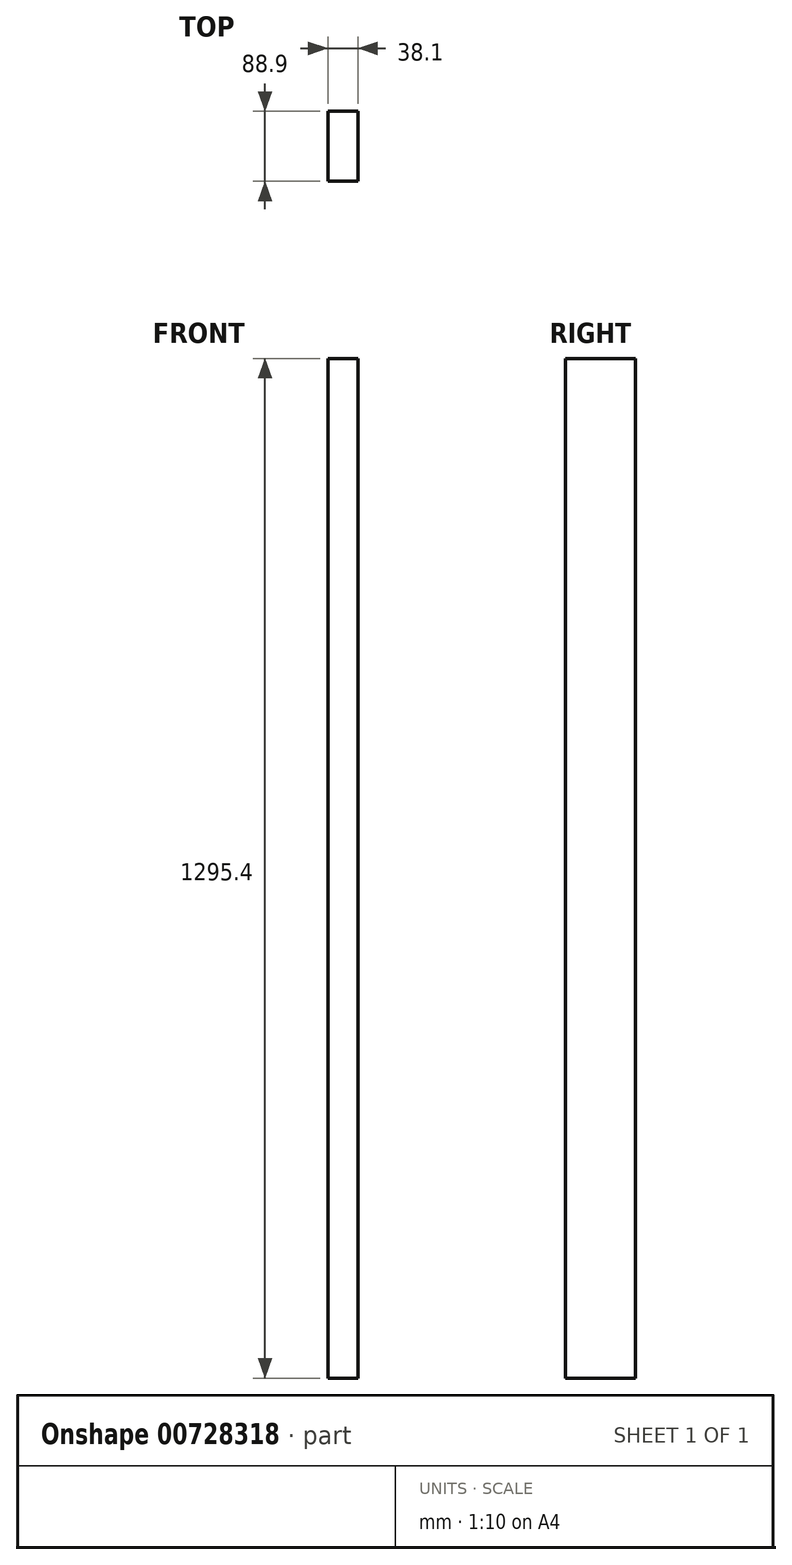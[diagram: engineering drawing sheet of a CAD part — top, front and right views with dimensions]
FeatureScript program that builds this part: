
annotation { "Feature Type Name" : "Feature", "Feature Type Description" : "" }
export const myFeature = defineFeature(function(context is Context, id is Id, definition is map)
    precondition{}
    {
        {
            var Q0;
            Q0=qCreatedBy(makeId("Front.planeOp"),FACE);
            var sketch = newSketch(context, id + "F0", { "sketchPlane" : qUnion([Q0])});
            skLineSegment(sketch, "E0.bottom", {"start": v(-19.05, -647.7) * mm, "end": v(19.05, -647.7) * mm});
            skLineSegment(sketch, "E0.top", {"start": v(-19.05, 647.7) * mm, "end": v(19.05, 647.7) * mm});
            skLineSegment(sketch, "E0.left", {"start": v(-19.05, -647.7) * mm, "end": v(-19.05, 647.7) * mm});
            skLineSegment(sketch, "E0.right", {"start": v(19.05, -647.7) * mm, "end": v(19.05, 647.7) * mm});
            skPoint(sketch, "E0.middle", {"position": v(0, 0) * mm});
            skSolve(sketch);
        }
        {
            var Q0;
            Q0=qSketchRegion(id+"F0",true);
            extrude(context, id + "F1", {"entities" : qUnion([Q0]), "depth" : 88.9 * mm});
        }
    });
